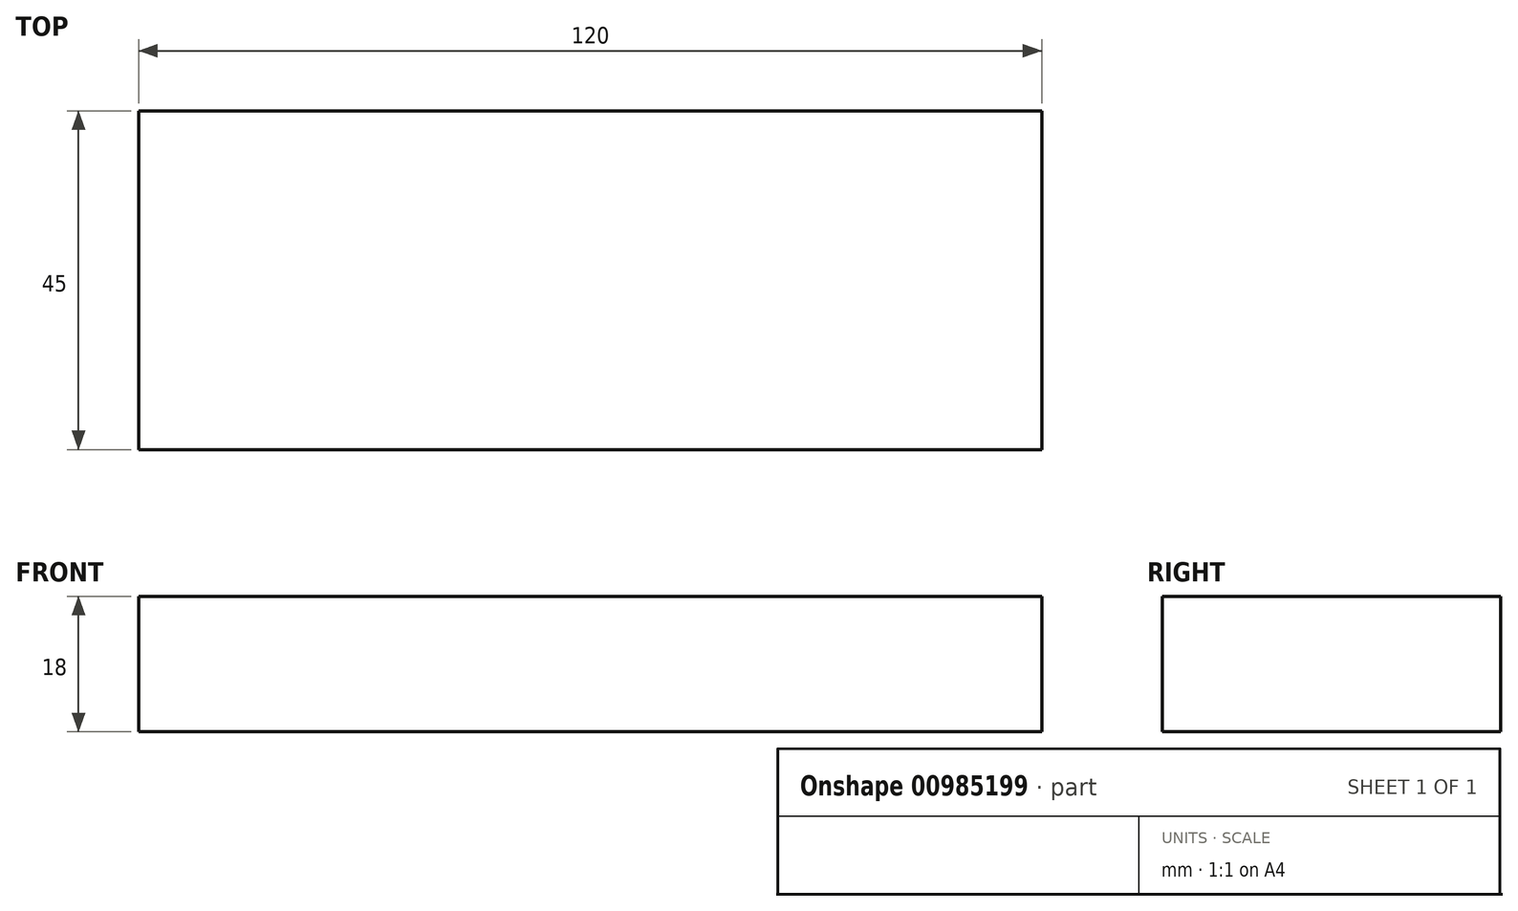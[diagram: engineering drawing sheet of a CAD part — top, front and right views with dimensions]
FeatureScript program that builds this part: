
annotation { "Feature Type Name" : "Feature", "Feature Type Description" : "" }
export const myFeature = defineFeature(function(context is Context, id is Id, definition is map)
    precondition{}
    {
        {
            var Q0;
            Q0=qCreatedBy(makeId("Top.planeOp"),FACE);
            var sketch = newSketch(context, id + "F0", { "sketchPlane" : qUnion([Q0])});
            skLineSegment(sketch, "E0.bottom", {"start": v(-60, 0) * mm, "end": v(60, 0) * mm});
            skLineSegment(sketch, "E0.top", {"start": v(-60, 45) * mm, "end": v(60, 45) * mm});
            skLineSegment(sketch, "E0.left", {"start": v(-60, 0) * mm, "end": v(-60, 45) * mm});
            skLineSegment(sketch, "E0.right", {"start": v(60, 0) * mm, "end": v(60, 45) * mm});
            skSolve(sketch);
        }
        {
            var Q0;
            Q0 = qSketchRegion(id + "F0", true);
            extrude(context, id + "F1", {"entities" : qUnion([Q0]), "depth" : 18 * mm, "offsetDistance" : 25 * mm});
        }
    });
